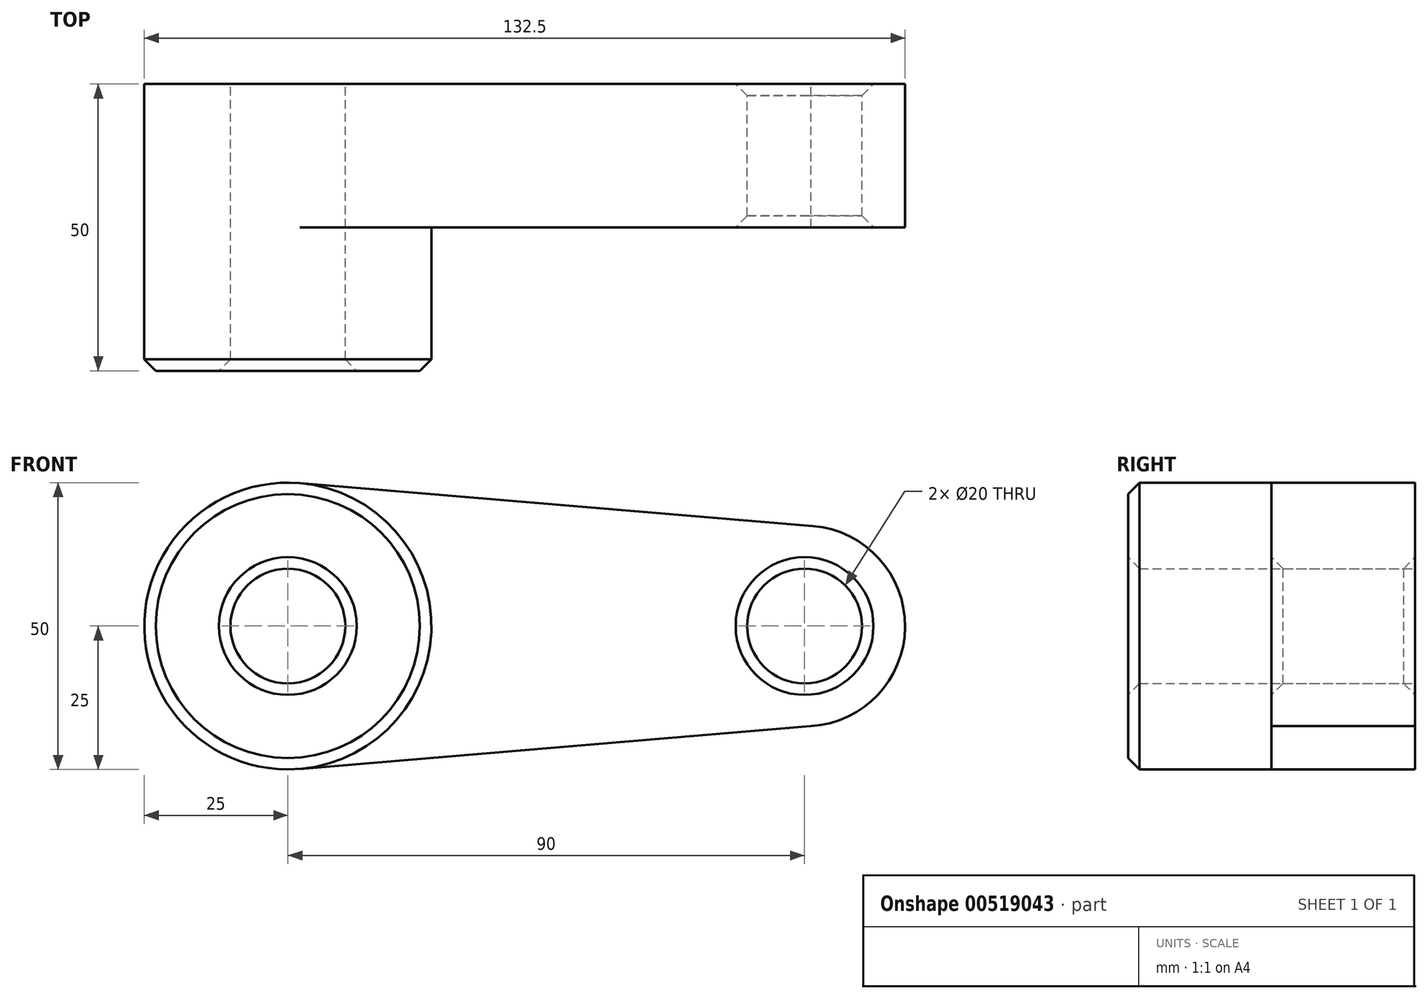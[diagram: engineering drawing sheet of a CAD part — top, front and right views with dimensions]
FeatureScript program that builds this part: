
annotation { "Feature Type Name" : "Feature", "Feature Type Description" : "" }
export const myFeature = defineFeature(function(context is Context, id is Id, definition is map)
    precondition{}
    {
        {
            var Q0;
            Q0=qCreatedBy(makeId("Front.planeOp"),FACE);
            var sketch = newSketch(context, id + "F0", { "sketchPlane" : qUnion([Q0])});
            skCircle(sketch, "E0", {"center": v(0, 0) * mm, "radius": 25 * mm});
            skCircle(sketch, "E1", {"center": v(90, 0) * mm, "radius": 17.5 * mm});
            skLineSegment(sketch, "E2", {"start": v(2.08, 24.91) * mm, "end": v(91.46, 17.44) * mm});
            skLineSegment(sketch, "E3", {"start": v(91.14, -17.46) * mm, "end": v(2.08, -24.91) * mm});
            skCircle(sketch, "E4", {"center": v(0, 0) * mm, "radius": 10 * mm});
            skCircle(sketch, "E5", {"center": v(90, 0) * mm, "radius": 10 * mm});
            skSolve(sketch);
        }
        {
            var Q0;
            Q0 = qSketchRegion(id + "F0", true);
            extrude(context, id + "F1", {"entities" : qUnion([Q0]), "depth" : 25 * mm, "offsetDistance" : 25 * mm});
        }
        {
            var Q0;
            Q0=makeQuery(id+"F0.imprint","IMPRINT",FACE,{"disambiguationData":[TD([[makeQuery(id+"F0.imprint","IMPRINT",EDGE,{"derivedFrom":sQuery(id+"F0.wireOp",EDGE,"E4")}),-1.0]])]});
            extrude(context, id + "F2", {"entities" : qUnion([Q0]), "operationType" : NewBodyOperationType.ADD, "depth" : 50 * mm, "offsetDistance" : 25 * mm});
        }
        {
            var Q0;
            Q0=makeQuery(id+"F2.opExtrude","CAP_FACE",FACE,{"disambiguationData":[OSD([sQuery(id+"F0.wireOp",EDGE,"E0"),sQuery(id+"F0.wireOp",EDGE,"E4")])],"isStart":false});
            var Q1;
            Q1=makeQuery(id+"F1.opExtrude","SWEPT_FACE",FACE,{"disambiguationData":[OSD([sQuery(id+"F0.wireOp",EDGE,"E5")])]});
            chamfer(context, id + "F3", {"entities" : qUnion([Q0, Q1]), "width" : 2 * mm, "tangentPropagation" : true});
        }
    });
